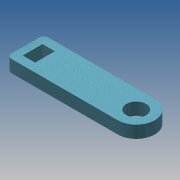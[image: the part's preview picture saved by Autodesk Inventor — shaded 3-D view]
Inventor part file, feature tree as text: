
AUTODESK INVENTOR PART (.ipt)
format: ipt  version: 2015 SP1 (Build 190203100, 203)  size: 131,584 bytes
history: native  units: mm
features: extrude x2, sketch x2, fillet x1, projected_geometry x1
ambient origin geometry x8: Origin, YZ Plane, XZ Plane, XY Plane, X Axis, Y Axis, Z Axis, Center Point
bodies: Volumenkörper1 (feature_tree)
feature tree (6):
  extrude  "Extrusion1"  Depth=3.5mm
  extrude  "Extrusion3"  Depth=2.0mm
  fillet  "Rundung1"  Radius=16.5mm
  sketch  "Skizze1"  dims[d0=3.5mm d1=15.5mm]
  sketch  "Skizze3"  dims[d2=15.5mm d3=22.0mm d4=16.5mm d5=11.0mm d6=8.0mm d7=15.0mm d10=15.0mm d11=45.0mm d12=5.0mm d13=0.0mm d17=5.0mm d18=8.0mm d19=3.0mm d20=5.0mm d21=0.0mm d22=2.0mm]
  projected_geometry  "Projizierte Kontur2"
